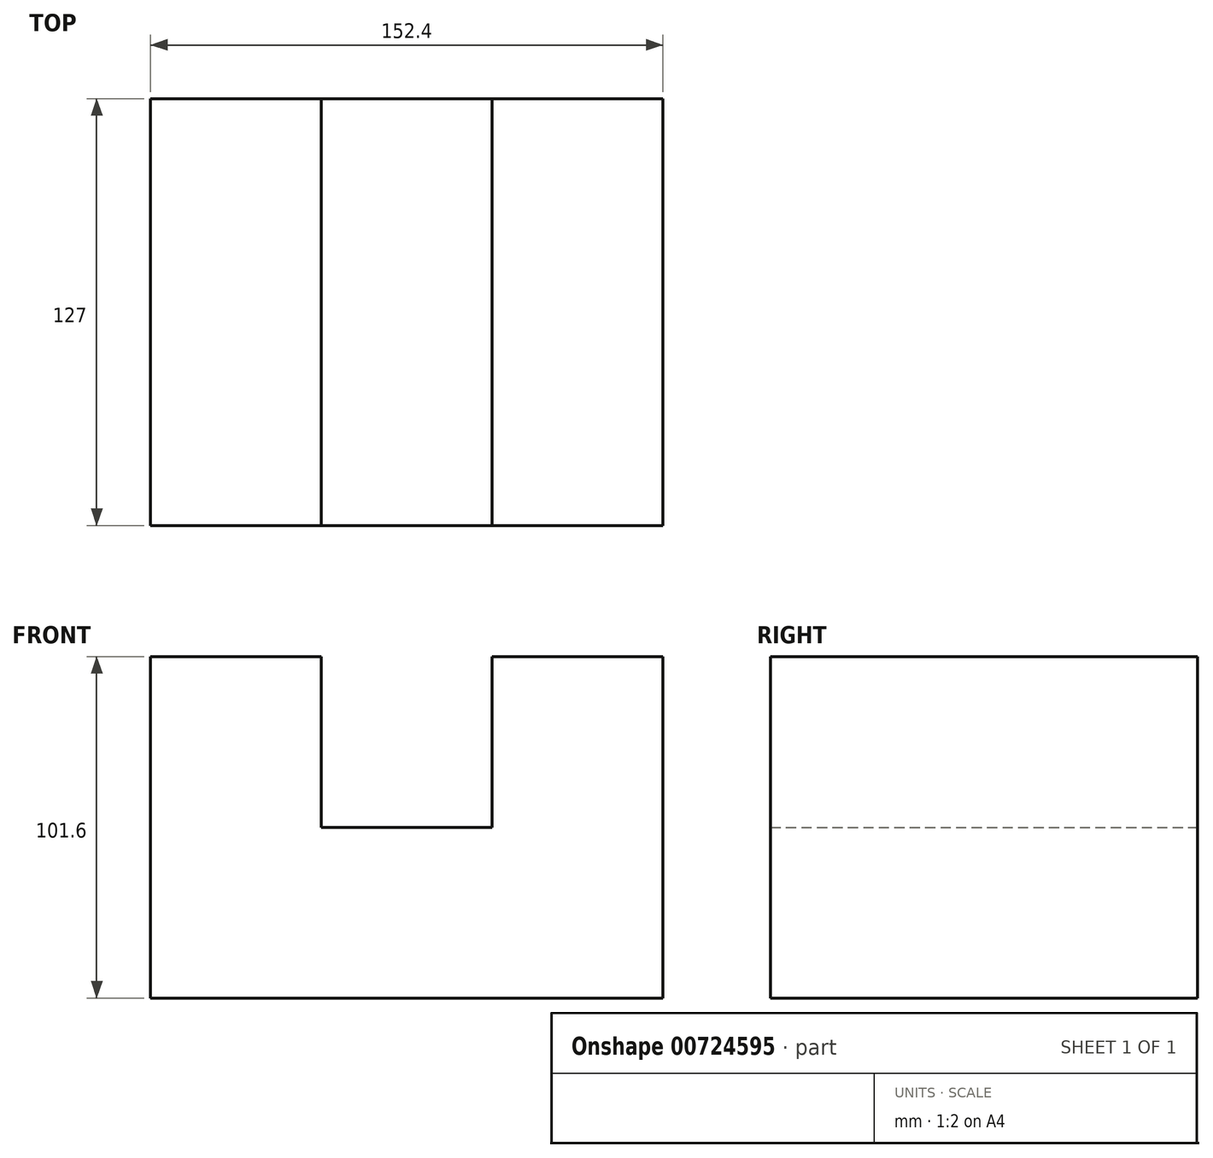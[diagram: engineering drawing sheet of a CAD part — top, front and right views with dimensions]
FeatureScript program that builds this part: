
annotation { "Feature Type Name" : "Feature", "Feature Type Description" : "" }
export const myFeature = defineFeature(function(context is Context, id is Id, definition is map)
    precondition{}
    {
        {
            var Q0;
            Q0=qCreatedBy(makeId("Front.planeOp"),FACE);
            var sketch = newSketch(context, id + "F0", { "sketchPlane" : qUnion([Q0])});
            skLineSegment(sketch, "E0", {"start": v(-76.8, -75.58) * mm, "end": v(75.6, -75.58) * mm});
            skLineSegment(sketch, "E1", {"start": v(75.6, -75.58) * mm, "end": v(75.6, 26.02) * mm});
            skLineSegment(sketch, "E2", {"start": v(75.6, 26.02) * mm, "end": v(24.8, 26.02) * mm});
            skLineSegment(sketch, "E3", {"start": v(24.8, 26.02) * mm, "end": v(24.8, -24.78) * mm});
            skLineSegment(sketch, "E4", {"start": v(24.8, -24.78) * mm, "end": v(-26, -24.78) * mm});
            skLineSegment(sketch, "E5", {"start": v(-26, -24.78) * mm, "end": v(-26, 26.02) * mm});
            skLineSegment(sketch, "E6", {"start": v(-26, 26.02) * mm, "end": v(-76.8, 26.02) * mm});
            skLineSegment(sketch, "E7", {"start": v(-76.8, 26.02) * mm, "end": v(-76.8, -75.58) * mm});
            skSolve(sketch);
        }
        {
            var Q0;
            Q0 = qSketchRegion(id + "F0", true);
            extrude(context, id + "F1", {"entities" : qUnion([Q0]), "depth" : 127 * mm, "offsetDistance" : 25.4 * mm});
        }
    });
